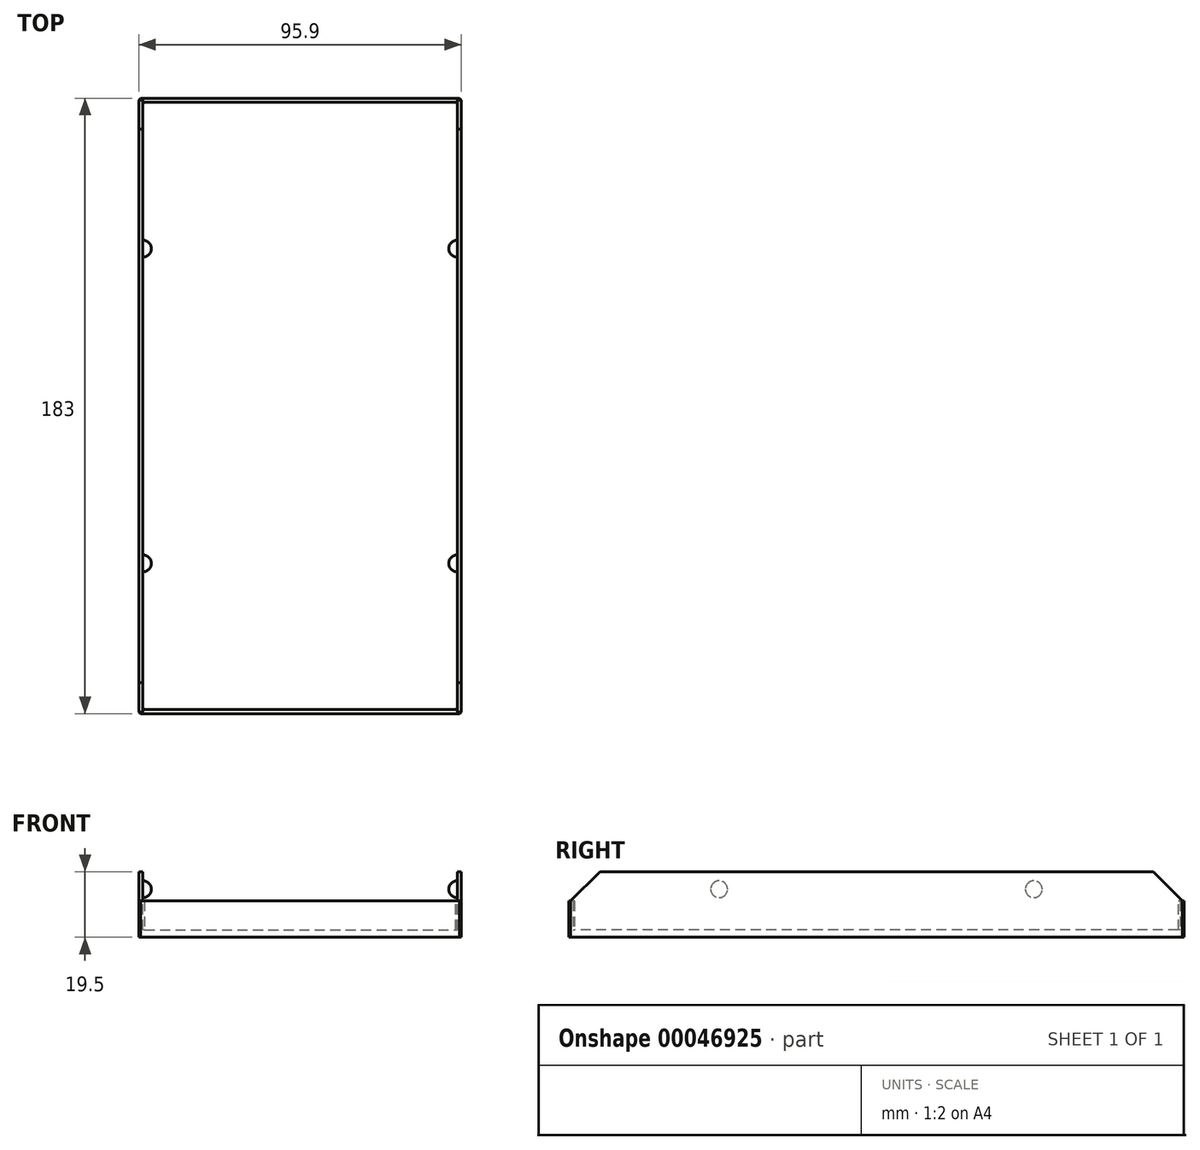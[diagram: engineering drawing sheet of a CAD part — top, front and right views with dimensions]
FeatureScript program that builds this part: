
annotation { "Feature Type Name" : "Feature", "Feature Type Description" : "" }
export const myFeature = defineFeature(function(context is Context, id is Id, definition is map)
    precondition{}
    {
        {
            var Q0;
            Q0=qCreatedBy(makeId("Top.planeOp"),FACE);
            var sketch = newSketch(context, id + "F0", { "sketchPlane" : qUnion([Q0])});
            skLineSegment(sketch, "E0.bottom", {"start": v(-34.06, 122.74) * mm, "end": v(61.84, 122.74) * mm});
            skLineSegment(sketch, "E0.top", {"start": v(-34.06, -60.26) * mm, "end": v(61.84, -60.26) * mm});
            skLineSegment(sketch, "E0.left", {"start": v(-34.06, 122.74) * mm, "end": v(-34.06, -60.26) * mm});
            skLineSegment(sketch, "E0.right", {"start": v(61.84, 122.74) * mm, "end": v(61.84, -60.26) * mm});
            skSolve(sketch);
        }
        {
            var Q0;
            Q0 = qSketchRegion(id + "F0", true);
            extrude(context, id + "F1", {"entities" : qUnion([Q0]), "depth" : 9.8 * mm});
        }
        {
            var Q0;
            Q0=makeQuery(id+"F1.opExtrude","CAP_FACE",FACE,{"disambiguationData":[OSD([sQuery(id+"F0.wireOp",EDGE,"E0.bottom"),sQuery(id+"F0.wireOp",EDGE,"E0.top"),sQuery(id+"F0.wireOp",EDGE,"E0.left"),sQuery(id+"F0.wireOp",EDGE,"E0.right")])],"isStart":false});
            shell(context, id + "F2", {"entities" : qUnion([Q0]), "thickness" : 1.2 * mm});
        }
        {
            var Q0;
            Q0=makeQuery(id+"F1.opExtrude","SWEPT_EDGE",EDGE,{"disambiguationData":[OSD([sQuery(id+"F0.wireOp",EDGE,"E0.top"),sQuery(id+"F0.wireOp",EDGE,"E0.right")])]});
            chamfer(context, id + "F3", {"entities" : qUnion([Q0]), "width" : 0.5 * mm, "tangentPropagation" : true});
        }
        {
            var Q0;
            Q0=makeQuery(id+"F1.opExtrude","SWEPT_EDGE",EDGE,{"disambiguationData":[OSD([sQuery(id+"F0.wireOp",EDGE,"E0.top"),sQuery(id+"F0.wireOp",EDGE,"E0.left")])]});
            chamfer(context, id + "F4", {"entities" : qUnion([Q0]), "width" : 0.5 * mm, "tangentPropagation" : true});
        }
        {
            var Q0;
            Q0=makeQuery(id+"F1.opExtrude","SWEPT_EDGE",EDGE,{"disambiguationData":[OSD([sQuery(id+"F0.wireOp",EDGE,"E0.bottom"),sQuery(id+"F0.wireOp",EDGE,"E0.left")])]});
            chamfer(context, id + "F5", {"entities" : qUnion([Q0]), "width" : 0.5 * mm, "tangentPropagation" : true});
        }
        {
            var Q0;
            Q0=makeQuery(id+"F1.opExtrude","SWEPT_EDGE",EDGE,{"disambiguationData":[OSD([sQuery(id+"F0.wireOp",EDGE,"E0.bottom"),sQuery(id+"F0.wireOp",EDGE,"E0.right")])]});
            chamfer(context, id + "F6", {"entities" : qUnion([Q0]), "width" : 0.5 * mm, "tangentPropagation" : true});
        }
        {
            var Q0;
            Q0=makeQuery(id+"F2.opShell","OFFSET_EDGE",EDGE,{"disambiguationData":[OSD([sQuery(id+"F0.wireOp",EDGE,"E0.bottom"),sQuery(id+"F0.wireOp",EDGE,"E0.right")])]});
            chamfer(context, id + "F7", {"entities" : qUnion([Q0]), "width" : 0.5 * mm, "tangentPropagation" : true});
        }
        {
            var Q0;
            Q0=makeQuery(id+"F2.opShell","OFFSET_EDGE",EDGE,{"disambiguationData":[OSD([sQuery(id+"F0.wireOp",EDGE,"E0.bottom"),sQuery(id+"F0.wireOp",EDGE,"E0.left")])]});
            chamfer(context, id + "F8", {"entities" : qUnion([Q0]), "width" : 0.5 * mm, "tangentPropagation" : true});
        }
        {
            var Q0;
            Q0=makeQuery(id+"F2.opShell","OFFSET_EDGE",EDGE,{"disambiguationData":[OSD([sQuery(id+"F0.wireOp",EDGE,"E0.top"),sQuery(id+"F0.wireOp",EDGE,"E0.right")])]});
            var Q1;
            Q1=makeQuery(id+"F2.opShell","OFFSET_EDGE",EDGE,{"disambiguationData":[OSD([sQuery(id+"F0.wireOp",EDGE,"E0.top"),sQuery(id+"F0.wireOp",EDGE,"E0.left")])]});
            chamfer(context, id + "F9", {"entities" : qUnion([Q0, Q1]), "width" : 0.5 * mm, "tangentPropagation" : true});
        }
        {
            var Q0;
            Q0=makeQuery(id+"F1.opExtrude","SWEPT_FACE",FACE,{"disambiguationData":[OSD([sQuery(id+"F0.wireOp",EDGE,"E0.right")])]});
            var sketch = newSketch(context, id + "F10", { "sketchPlane" : qUnion([Q0])});
            skLineSegment(sketch, "E1.bottom", {"start": v(-59.76, 9.8) * mm, "end": v(122.24, 9.8) * mm});
            skLineSegment(sketch, "E1.top", {"start": v(-51.06, 18.5) * mm, "end": v(113.54, 18.5) * mm});
            skPoint(sketch, "E2", {"position": v(113.54, 18.5) * mm});
            skLineSegment(sketch, "E3", {"start": v(113.54, 18.5) * mm, "end": v(122.24, 9.8) * mm});
            skPoint(sketch, "E1.right.end.orphan", {"position": v(122.24, 18.5) * mm});
            skPoint(sketch, "E4", {"position": v(-51.06, 18.5) * mm});
            skLineSegment(sketch, "E5", {"start": v(-51.06, 18.5) * mm, "end": v(-59.76, 9.8) * mm});
            skPoint(sketch, "E1.left.end.orphan", {"position": v(-59.76, 18.5) * mm});
            skSolve(sketch);
        }
        {
            var Q0;
            Q0 = qSketchRegion(id + "F10", true);
            var Q1;
            Q1=makeQuery(id+"F2.opShell","OFFSET_FACE",FACE,{"disambiguationData":[OSD([sQuery(id+"F0.wireOp",EDGE,"E0.right")])]});
            extrude(context, id + "F11", {"entities" : qUnion([Q0]), "operationType" : NewBodyOperationType.ADD, "endBound" : BoundingType.UP_TO_SURFACE, "oppositeDirection" : true, "endBoundEntityFace" : qUnion([Q1]), "depth" : 25 * mm});
        }
        {
            var Q0;
            Q0=makeQuery(id+"F1.opExtrude","SWEPT_FACE",FACE,{"disambiguationData":[OSD([sQuery(id+"F0.wireOp",EDGE,"E0.left")])]});
            var sketch = newSketch(context, id + "F12", { "sketchPlane" : qUnion([Q0])});
            skLineSegment(sketch, "E6", {"start": v(-113.54, 18.5) * mm, "end": v(51.06, 18.5) * mm});
            skLineSegment(sketch, "E7", {"start": v(59.76, 9.8) * mm, "end": v(-122.24, 9.8) * mm});
            skPoint(sketch, "E8", {"position": v(51.06, 18.5) * mm});
            skLineSegment(sketch, "E9", {"start": v(51.06, 18.5) * mm, "end": v(59.76, 9.8) * mm});
            skPoint(sketch, "E10.start.orphan", {"position": v(59.76, 18.5) * mm});
            skPoint(sketch, "E11", {"position": v(-113.54, 18.5) * mm});
            skLineSegment(sketch, "E12", {"start": v(-122.24, 9.8) * mm, "end": v(-113.54, 18.5) * mm});
            skPoint(sketch, "E13.end.orphan", {"position": v(-122.24, 18.5) * mm});
            skSolve(sketch);
        }
        {
            var Q0;
            Q0 = qSketchRegion(id + "F12", true);
            var Q1;
            Q1=makeQuery(id+"F2.opShell","OFFSET_FACE",FACE,{"disambiguationData":[OSD([sQuery(id+"F0.wireOp",EDGE,"E0.left")])]});
            extrude(context, id + "F13", {"entities" : qUnion([Q0]), "operationType" : NewBodyOperationType.ADD, "endBound" : BoundingType.UP_TO_SURFACE, "oppositeDirection" : true, "endBoundEntityFace" : qUnion([Q1]), "depth" : 25 * mm});
        }
        {
            var Q0;
            Q0=makeQuery(id+"F13.boolean.opBoolean","MERGE",FACE,{"derivedFrom":[makeQuery(id+"F2.opShell","OFFSET_FACE",FACE,{"disambiguationData":[OSD([sQuery(id+"F0.wireOp",EDGE,"E0.left")])]}),makeQuery(id+"F13.opExtrude","CAP_FACE",FACE,{"disambiguationData":[OSD([sQuery(id+"F12.wireOp",EDGE,"E6"),sQuery(id+"F12.wireOp",EDGE,"E7"),sQuery(id+"F12.wireOp",EDGE,"E9"),sQuery(id+"F12.wireOp",EDGE,"E12")])],"isStart":false})]});
            var sketch = newSketch(context, id + "F14", { "sketchPlane" : qUnion([Q0])});
            skPoint(sketch, "E14", {"position": v(-15.56, 13.3) * mm});
            skCircle(sketch, "E15", {"center": v(-15.56, 13.3) * mm, "radius": 2.5 * mm});
            skLineSegment(sketch, "E16", {"start": v(-15.56, 13.3) * mm, "end": v(-13.06, 13.3) * mm});
            skLineSegment(sketch, "E17", {"start": v(-15.56, 13.3) * mm, "end": v(-18.06, 13.3) * mm});
            skPoint(sketch, "E18", {"position": v(78.04, 13.3) * mm});
            skCircle(sketch, "E19", {"center": v(78.04, 13.3) * mm, "radius": 2.5 * mm});
            skLineSegment(sketch, "E20", {"start": v(78.04, 13.3) * mm, "end": v(80.54, 13.3) * mm});
            skLineSegment(sketch, "E21", {"start": v(78.04, 13.3) * mm, "end": v(75.54, 13.3) * mm});
            skSolve(sketch);
        }
        {
            var Q0;
            {var subQ1=sQuery(id+"F14.wireOp",EDGE,"E16");Q0=makeQuery(id+"F14.imprint","IMPRINT",FACE,{"disambiguationData":[TD([[makeQuery(id+"F14.imprint","IMPRINT",EDGE,{"derivedFrom":subQ1}),1.0]])]});}
            var Q1;
            Q1=sQuery(id+"F14.wireOp",EDGE,"E16");
            revolve(context, id + "F15", {"operationType" : NewBodyOperationType.ADD, "entities" : qUnion([Q0]), "axis" : qUnion([Q1]), "revolveType" : RevolveType.ONE_DIRECTION, "angle" : 180 * degree});
        }
        {
            var Q0;
            {var subQ1=sQuery(id+"F14.wireOp",EDGE,"E20");Q0=makeQuery(id+"F14.imprint","IMPRINT",FACE,{"disambiguationData":[TD([[makeQuery(id+"F14.imprint","IMPRINT",EDGE,{"derivedFrom":subQ1}),1.0]])]});}
            var Q1;
            Q1=sQuery(id+"F14.wireOp",EDGE,"E20");
            revolve(context, id + "F16", {"operationType" : NewBodyOperationType.ADD, "entities" : qUnion([Q0]), "axis" : qUnion([Q1]), "revolveType" : RevolveType.ONE_DIRECTION, "angle" : 180 * degree});
        }
        {
            var Q0;
            Q0=makeQuery(id+"F11.boolean.opBoolean","MERGE",FACE,{"derivedFrom":[makeQuery(id+"F2.opShell","OFFSET_FACE",FACE,{"disambiguationData":[OSD([sQuery(id+"F0.wireOp",EDGE,"E0.right")])]}),makeQuery(id+"F11.opExtrude","CAP_FACE",FACE,{"disambiguationData":[OSD([sQuery(id+"F10.wireOp",EDGE,"E1.bottom"),sQuery(id+"F10.wireOp",EDGE,"E1.top"),sQuery(id+"F10.wireOp",EDGE,"E3"),sQuery(id+"F10.wireOp",EDGE,"E5")])],"isStart":false})]});
            var sketch = newSketch(context, id + "F17", { "sketchPlane" : qUnion([Q0])});
            skPoint(sketch, "E22", {"position": v(-78.04, 13.3) * mm});
            skPoint(sketch, "E23", {"position": v(15.56, 13.3) * mm});
            skCircle(sketch, "E24", {"center": v(-78.04, 13.3) * mm, "radius": 2.5 * mm});
            skCircle(sketch, "E25", {"center": v(15.56, 13.3) * mm, "radius": 2.5 * mm});
            skLineSegment(sketch, "E26", {"start": v(-78.04, 13.3) * mm, "end": v(-80.54, 13.3) * mm});
            skLineSegment(sketch, "E27", {"start": v(-78.04, 13.3) * mm, "end": v(-75.54, 13.3) * mm});
            skLineSegment(sketch, "E28", {"start": v(15.56, 13.3) * mm, "end": v(18.06, 13.3) * mm});
            skLineSegment(sketch, "E29", {"start": v(15.56, 13.3) * mm, "end": v(13.06, 13.3) * mm});
            skSolve(sketch);
        }
        {
            var Q0;
            {var subQ0=sQuery(id+"F17.wireOp",EDGE,"E26");Q0=makeQuery(id+"F17.imprint","IMPRINT",FACE,{"disambiguationData":[TD([[makeQuery(id+"F17.imprint","IMPRINT",EDGE,{"derivedFrom":subQ0}),-1.0]])]});}
            var Q1;
            Q1=sQuery(id+"F17.wireOp",EDGE,"E27");
            revolve(context, id + "F18", {"operationType" : NewBodyOperationType.ADD, "entities" : qUnion([Q0]), "axis" : qUnion([Q1]), "revolveType" : RevolveType.ONE_DIRECTION, "angle" : 180 * degree});
        }
        {
            var Q0;
            {var subQ0=sQuery(id+"F17.wireOp",EDGE,"E28");Q0=makeQuery(id+"F17.imprint","IMPRINT",FACE,{"disambiguationData":[TD([[makeQuery(id+"F17.imprint","IMPRINT",EDGE,{"derivedFrom":subQ0}),1.0]])]});}
            var Q1;
            Q1=sQuery(id+"F17.wireOp",EDGE,"E28");
            revolve(context, id + "F19", {"operationType" : NewBodyOperationType.ADD, "entities" : qUnion([Q0]), "axis" : qUnion([Q1]), "revolveType" : RevolveType.ONE_DIRECTION, "angle" : 180 * degree});
        }
        {
            var Q0;
            Q0=makeQuery(id+"F1.opExtrude","CAP_FACE",FACE,{"disambiguationData":[OSD([sQuery(id+"F0.wireOp",EDGE,"E0.bottom"),sQuery(id+"F0.wireOp",EDGE,"E0.top"),sQuery(id+"F0.wireOp",EDGE,"E0.left"),sQuery(id+"F0.wireOp",EDGE,"E0.right")])],"isStart":true});
            extrude(context, id + "F20", {"entities" : qUnion([Q0]), "operationType" : NewBodyOperationType.ADD, "depth" : 1 * mm});
        }
    });
